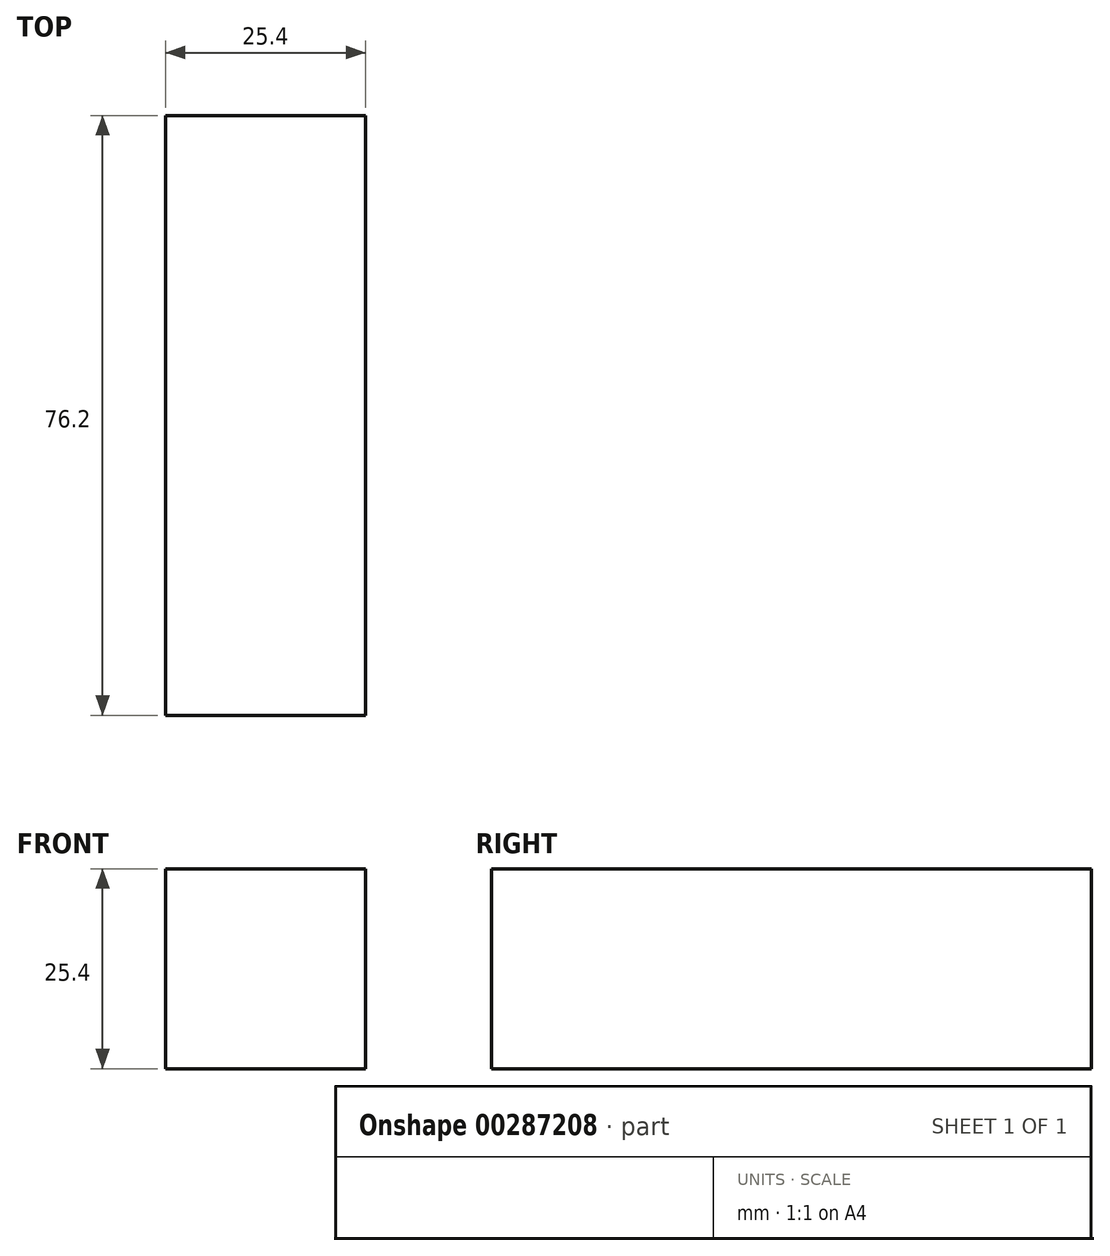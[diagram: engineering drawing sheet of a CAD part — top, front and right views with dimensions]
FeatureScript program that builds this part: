
annotation { "Feature Type Name" : "Feature", "Feature Type Description" : "" }
export const myFeature = defineFeature(function(context is Context, id is Id, definition is map)
    precondition{}
    {
        {
            var Q0;
            Q0=qCreatedBy(makeId("Front.planeOp"),FACE);
            var sketch = newSketch(context, id + "F0", { "sketchPlane" : qUnion([Q0])});
            skLineSegment(sketch, "E0.bottom", {"start": v(-50.22, 12.22) * mm, "end": v(-24.82, 12.22) * mm});
            skLineSegment(sketch, "E0.top", {"start": v(-50.22, 37.62) * mm, "end": v(-24.82, 37.62) * mm});
            skLineSegment(sketch, "E0.left", {"start": v(-50.22, 12.22) * mm, "end": v(-50.22, 37.62) * mm});
            skLineSegment(sketch, "E0.right", {"start": v(-24.82, 12.22) * mm, "end": v(-24.82, 37.62) * mm});
            skSolve(sketch);
        }
        {
            var Q0;
            Q0 = qSketchRegion(id + "F0", true);
            extrude(context, id + "F1", {"entities" : qUnion([Q0]), "depth" : 76.2 * mm});
        }
    });
